# Revit family: PlumbingFixture_Valve_AVG_TMV20BP-PIB
name_source: partatom
category: Plumbing Fixtures
revit_build: Autodesk Revit 2017 (Build: 20190508_0315(x64)
units: mm (PartAtom-declared; Revit-internal decimal feet)

## family parameters
Cut with Voids When Loaded = No
Host = Face
Part Type = Normal
Room Calculation Point = No
Round Connector Dimension = Use Diameter
Shared = No

## types (1)
- Type 1
    Adjustable_Mixed-Outlet_Temp (°C ) = 35-45
    Bypass_Size = 20 mm  [stored 0.0656168 ft]
    Bypass_Type = Tube
    CW Connection = No
    Cold_Water_Supply_Temp (°C ) = 5-25
    Comments_For_Revit = Same basic Valve (TMV20 & TVA20)
    Default Elevation = 0 mm  [stored 0 ft]
    Description = Thermostatic mixing valve supplied with right angle ball valves. Loose nut and tail connection to valve. Plumbed in stainless steel box, with cold water bypass. Copper tube tails.
    Factory_Set_Mixed_Temp (°C ) = 40
    HW Connection = No
    Hot_Water_Supply_Temp (°C ) = 60-85
    Inlet_Size_CW = 20 mm  [stored 0.0656168 ft]
    Inlet_Size_HW = 20 mm  [stored 0.0656168 ft]
    Inlet_Type = Tube
    Manufacturer = Australian Valve Group
    Max_Flow_Rate (l/min) = 27
    Max_Supply_Pressure_Dynamic (kPa) = 500
    Max_Supply_Pressure_Static (kPa) = 1000
    Min_Supply_Pressure_Dynamic (kPa) = 20
    Min_Supply_Pressure_Imbalance (%) = 10
    Min_Temp_Differential_Cold_to_Mixed (°C ) = 5
    Min_Temp_Differential_Hot_to_Mixed (°C ) = 10
    Minimum_Flow_Rate (l/min) = 4
    Outlet_Size = 20 mm  [stored 0.0656168 ft]
    Outlet_Type = Tube
    Plumbed_In_Box_Dimensions(mm) = 350 x 350 x 75 deep
    PlumbingMaterial_ANZRS = <By Category>
    Product_Type = TMV20BP-PIB
    Specify_Host = Face
    Tolerance_Mixed-Outlet_Temp (°C ) = ±2
    URL = https://www.avg.net.au
    Valve_Model = TMV20
    Vent Connection = No
    Waste Connection = No

note: [stored X ft] marks values corroborated as IEEE doubles in the binary element streams (Revit-internal decimal feet)

## geometry (parser evidence)
native form markers: Sweep x34
no freeform markers — native parametric forms only
